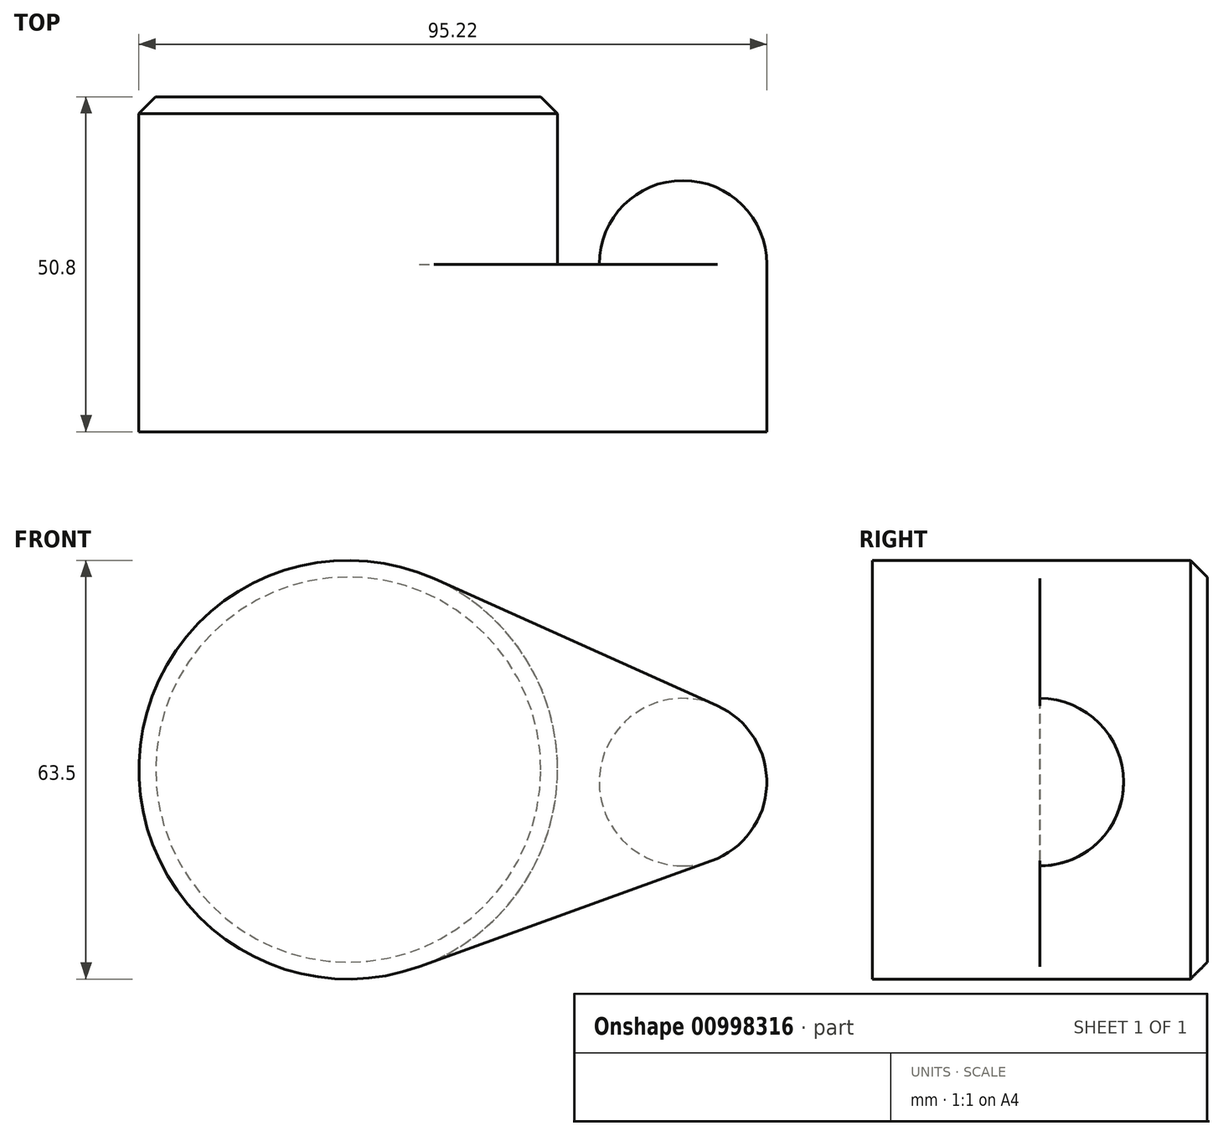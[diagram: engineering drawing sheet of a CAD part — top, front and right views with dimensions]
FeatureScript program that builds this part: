
annotation { "Feature Type Name" : "Feature", "Feature Type Description" : "" }
export const myFeature = defineFeature(function(context is Context, id is Id, definition is map)
    precondition{}
    {
        {
            var Q0;
            Q0=qCreatedBy(makeId("Front.planeOp"),FACE);
            var sketch = newSketch(context, id + "F0", { "sketchPlane" : qUnion([Q0])});
            skCircle(sketch, "E0", {"center": v(-62.6, 21.26) * mm, "radius": 31.75 * mm});
            skCircle(sketch, "E1", {"center": v(-11.84, 19.37) * mm, "radius": 12.7 * mm});
            skLineSegment(sketch, "E2", {"start": v(-49.61, 50.23) * mm, "end": v(-6.64, 30.96) * mm});
            skLineSegment(sketch, "E3", {"start": v(-51.8, -8.6) * mm, "end": v(-7.52, 7.43) * mm});
            skSolve(sketch);
        }
        {
            var Q0;
            Q0 = qSketchRegion(id + "F0", true);
            extrude(context, id + "F1", {"entities" : qUnion([Q0]), "depth" : 25.4 * mm, "offsetDistance" : 25.4 * mm});
        }
        {
            var Q0;
            {var subQ0=sQuery(id+"F0.wireOp",EDGE,"E0");var subQ1=makeQuery(id+"F0.imprint","INTERSECT",VERTEX,{"derivedFrom":[subQ0,sQuery(id+"F0.wireOp",EDGE,"E2")]});Q0=makeQuery(id+"F0.imprint","IMPRINT",FACE,{"disambiguationData":[TD([[makeQuery(id+"F0.imprint","IMPRINT",EDGE,{"disambiguationData":[TD([[subQ1,-1.0]])],"derivedFrom":subQ0}),1.0]])]});}
            extrude(context, id + "F2", {"entities" : qUnion([Q0]), "operationType" : NewBodyOperationType.ADD, "oppositeDirection" : true, "depth" : 25.4 * mm, "offsetDistance" : 25.4 * mm});
        }
        {
            var Q0;
            {var subQ0=sQuery(id+"F0.wireOp",EDGE,"E1");var subQ1=makeQuery(id+"F0.imprint","INTERSECT",VERTEX,{"derivedFrom":[subQ0,sQuery(id+"F0.wireOp",EDGE,"E2")]});Q0=makeQuery(id+"F0.imprint","IMPRINT",FACE,{"disambiguationData":[TD([[makeQuery(id+"F0.imprint","IMPRINT",EDGE,{"disambiguationData":[TD([[subQ1,-1.0]])],"derivedFrom":subQ0}),1.0]])]});}
            extrude(context, id + "F3", {"entities" : qUnion([Q0]), "operationType" : NewBodyOperationType.ADD, "oppositeDirection" : true, "depth" : 12.7 * mm, "offsetDistance" : 25.4 * mm});
        }
        {
            var Q0;
            Q0=makeQuery(id+"F3.opExtrude","CAP_EDGE",EDGE,{"disambiguationData":[OSD([sQuery(id+"F0.wireOp",EDGE,"E1")])],"isStart":false});
            fillet(context, id + "F4", {"entities" : qUnion([Q0]), "radius" : 12.7 * mm, "tangentPropagation" : true, "allowEdgeOverflow" : false});
        }
        {
            var Q0;
            Q0=makeQuery(id+"F2.opExtrude","CAP_EDGE",EDGE,{"disambiguationData":[OSD([sQuery(id+"F0.wireOp",EDGE,"E0")])],"isStart":false});
            chamfer(context, id + "F5", {"entities" : qUnion([Q0]), "width" : 2.54 * mm, "tangentPropagation" : true});
        }
    });
